# Revit family: QF_Macom_RVCx
name_source: partatom
category: Specialty Equipment
units: mm (PartAtom-declared; Revit-internal decimal feet)

## family parameters
Always vertical = Yes
Cut with Voids When Loaded = No
OmniClass Number = 23.40.40.11.11.11
OmniClass Title = Refrigerators
Part Type = Normal
Room Calculation Point = No
Round Connector Dimension = Use Diameter
Shared = No
Work Plane-Based = No

## types (8) — shared parameters
Cycle = 60 Hz
Default Elevation = 0 mm
Depth Actual = 800 mm
Door Width = 672 mm
Door1 = Yes
Drain Size = 3/4"
Elec Conn Connection Height = 1823 mm
Half_Glass_Half_Stainless = No
Height Actual = 2070 mm
Ingress Protection Code = IP 22
Manufacturer = MACOM
Refrigerant Type = R134a
Refrigeration Climate Class = 5
URL = https://www.acosmacom.com.br
Volts = 220 V
Work Temperature = +1°C to +10°C

## per-type parameters (varying)
| type | Capacity | Description | Door QTY | Door2 | Full_Glass_Door | Full_Stainless_Door | Half_Glass_Door | Half_Stainless_Door | Length Actual | Model | Operational Current | Phase | Volume | Watts | Weight |
| RVCD-1I_ | 1280 L | REFRIG VERTICAL COMERCIAL DUPLO MACOM, 2 PORTAS INOX E 8 GRADES -1400X800X2070 | 2 | Yes | No | Yes | No | No | 1400 mm | RVCD-2I_ | 5 A | 0 | 2,32 m³ | 778 W | 220,00 kg |
| RVCS-1V_ | 580 L | REFRIG VERTICAL COMERCIAL SIMPLES MACOM 1 PORTA VIDRO 12 TRILHOS E ILUMINACAO-700X800X2070 | 1 | No | Yes | No | No | No | 700 mm | RVCS-1V_ | 3 A | 1 | 1,16 m³ | 465 W | 125,00 kg |
| RVCD-2I_ | 1280 L | REFRIG VERTICAL COMERCIAL DUPLO MACOM, 4 PORTAS INOX E 8 GRADES - 1400X805X2070 | 2 | Yes | No | No | No | Yes | 1400 mm | RVCD-4IG | 5 A | 0 | 2,32 m³ | 778 W | 220,00 kg |
| RVCS-2I_ | 580 L | REFRIG VERTICAL COMERCIAL SIMPLES MACOM, 2 PORTAS INOX E 4 GRADES -700X800X2070 | 1 | No | No | No | No | Yes | 700 mm | RVCS-2I_ | 3 A | 0 | 1,16 m³ | 465 W | 125,00 kg |
| RVCS-2V_ | 580 L | REFRIG VERTICAL COMERCIAL SIMPLES MACOM, 2 PORTAS  VIDRO - 700X800X2070 | 1 | No | No | No | Yes | No | 700 mm | RVCS-2V_ | 3 A | 1 | 1,16 m³ | 465 W | 125,00 kg |
| RVCS-1I_ | 580 L | REFRIG VERTICAL COMERCIAL SIMPLES MACOM 1 PORTA INOX -700X800X2070 | 1 | No | No | Yes | No | No | 700 mm | RVCS-1I_ | 3 A | 1 | 1,16 m³ | 465 W | 125,00 kg |
| RVCD-1V_ | 1280 L | REFRIG VERTICAL COMERCIAL DUPLO MACOM, 2 PORTAS VIDRO-1400X800X2070 | 2 | Yes | Yes | No | No | No | 1400 mm | RVCD-1V_ | 5 A | 0 | 2,32 m³ | 778 W | 220,00 kg |
| RVCD-2V_ | 1280 L | REFRIG VERTICAL COMERCIAL DUPLO MACOM, 4 PORTAS VIDRO- 1400X805X2070 | 2 | Yes | No | No | Yes | No | 1400 mm | RVCD-2V_ | 5 A | 0 | 2,32 m³ | 778 W | 220,00 kg |

## geometry (parser evidence)
native form markers: Sweep x5
no freeform markers — native parametric forms only
